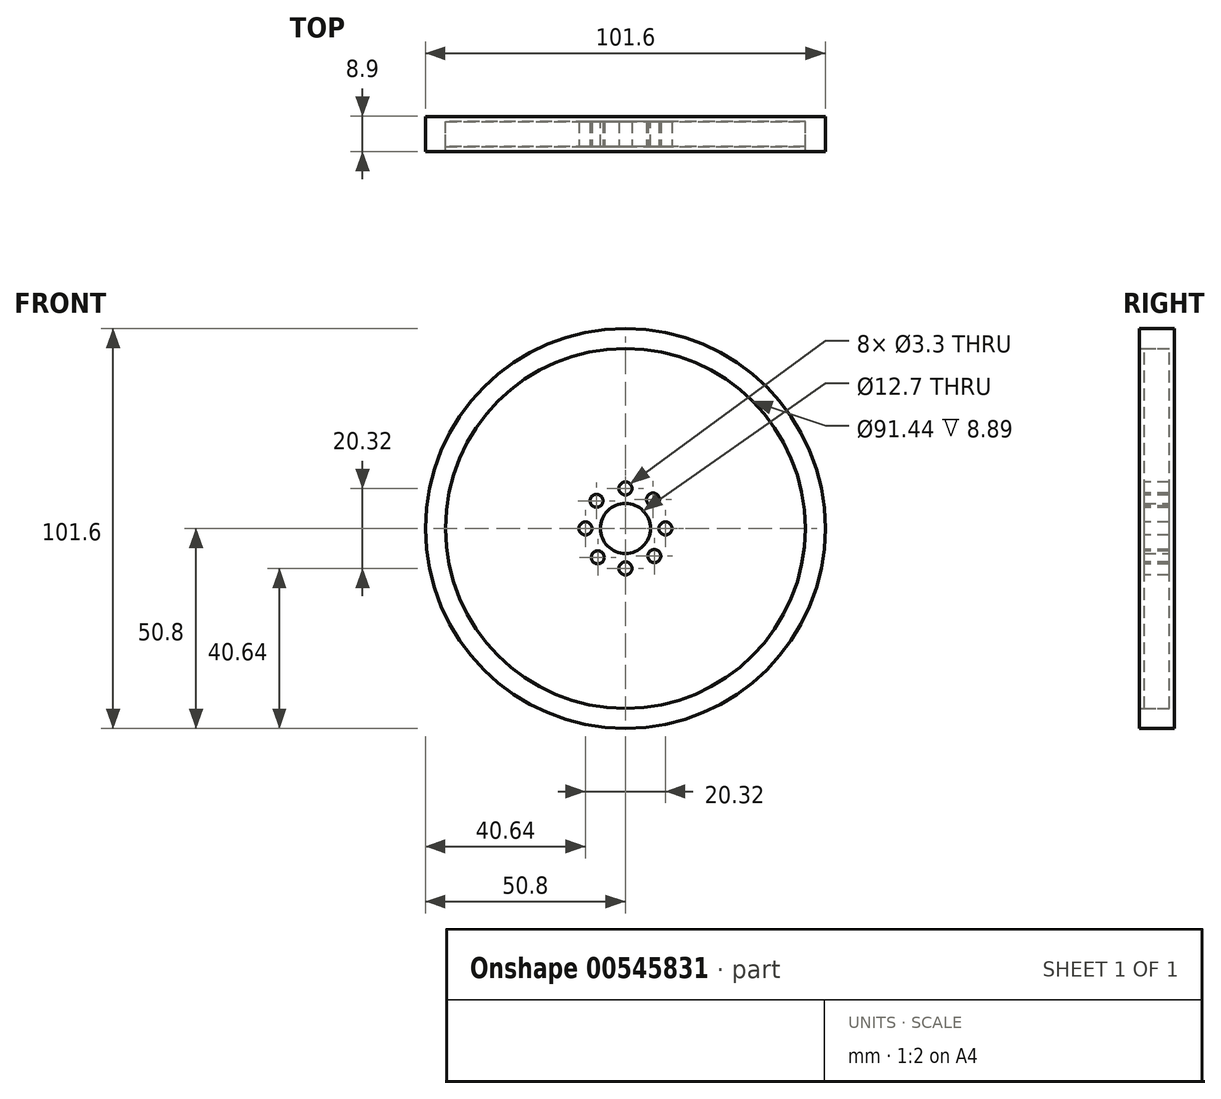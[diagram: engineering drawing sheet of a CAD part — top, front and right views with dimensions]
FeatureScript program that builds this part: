
annotation { "Feature Type Name" : "Feature", "Feature Type Description" : "" }
export const myFeature = defineFeature(function(context is Context, id is Id, definition is map)
    precondition{}
    {
        {
            var Q0;
            Q0=qCreatedBy(makeId("Front.planeOp"),FACE);
            var sketch = newSketch(context, id + "F0", { "sketchPlane" : qUnion([Q0])});
            skCircle(sketch, "E0", {"center": v(0, 0) * mm, "radius": 45.72 * mm});
            skCircle(sketch, "E1", {"center": v(0, 0) * mm, "radius": 50.8 * mm});
            skCircle(sketch, "E2", {"center": v(0, 0) * mm, "radius": 6.35 * mm});
            skSolve(sketch);
        }
        {
            var Q0;
            Q0=makeQuery(id+"F0.imprint","IMPRINT",FACE,{"disambiguationData":[TD([[makeQuery(id+"F0.imprint","IMPRINT",EDGE,{"derivedFrom":sQuery(id+"F0.wireOp",EDGE,"E0")}),-1.0]])]});
            extrude(context, id + "F1", {"entities" : qUnion([Q0]), "depth" : 8.9 * mm, "offsetDistance" : 25.4 * mm, "symmetric" : true});
        }
        {
            var Q0;
            Q0=makeQuery(id+"F0.imprint","IMPRINT",FACE,{"disambiguationData":[TD([[makeQuery(id+"F0.imprint","IMPRINT",EDGE,{"derivedFrom":sQuery(id+"F0.wireOp",EDGE,"E0")}),1.0]])]});
            extrude(context, id + "F2", {"entities" : qUnion([Q0]), "depth" : 6.35 * mm, "offsetDistance" : 25.4 * mm, "symmetric" : true});
        }
        {
            var Q0;
            Q0=makeQuery(id+"F2.opExtrude","CAP_FACE",FACE,{"disambiguationData":[OSD([sQuery(id+"F0.wireOp",EDGE,"E0"),sQuery(id+"F0.wireOp",EDGE,"E2")])],"isStart":false});
            var sketch = newSketch(context, id + "F3", { "sketchPlane" : qUnion([Q0])});
            skCircle(sketch, "E3", {"center": v(0, 0) * mm, "radius": 10.16 * mm, "construction": true});
            skPoint(sketch, "E4", {"position": v(0, 10.16) * mm});
            skPoint(sketch, "E5.2.0", {"position": v(7.02, 7.34) * mm});
            skPoint(sketch, "E6", {"position": v(10.16, 0) * mm});
            skPoint(sketch, "E7", {"position": v(0, -10.16) * mm});
            skPoint(sketch, "E8", {"position": v(-10.16, 0) * mm});
            skPoint(sketch, "E9.1.0", {"position": v(7.34, -7.02) * mm});
            skPoint(sketch, "E10.2.0", {"position": v(-7.02, -7.34) * mm});
            skPoint(sketch, "E11.1.0", {"position": v(-7.34, 7.02) * mm});
            skLineSegment(sketch, "E12", {"start": v(-7.02, -7.34) * mm, "end": v(0, 0) * mm, "construction": true});
            skLineSegment(sketch, "E13", {"start": v(-7.34, 7.02) * mm, "end": v(0, 0) * mm, "construction": true});
            skLineSegment(sketch, "E14", {"start": v(7.02, 7.34) * mm, "end": v(0, 0) * mm, "construction": true});
            skLineSegment(sketch, "E15", {"start": v(0, 0) * mm, "end": v(7.34, -7.02) * mm, "construction": true});
            skSolve(sketch);
        }
        {
            var Q0;
            Q0=sQuery(id+"F3.wireOp",VERTEX,"E6");
            var Q1;
            Q1=sQuery(id+"F3.wireOp",VERTEX,"E9.1.0");
            var Q2;
            Q2=sQuery(id+"F3.wireOp",VERTEX,"E9.2.0");
            var Q3;
            Q3=sQuery(id+"F3.wireOp",VERTEX,"E7");
            var Q4;
            Q4=sQuery(id+"F3.wireOp",VERTEX,"E10.1.0");
            var Q5;
            Q5=sQuery(id+"F3.wireOp",VERTEX,"E10.2.0");
            var Q6;
            Q6=sQuery(id+"F3.wireOp",VERTEX,"E8");
            var Q7;
            Q7=sQuery(id+"F3.wireOp",VERTEX,"E11.1.0");
            var Q8;
            Q8=sQuery(id+"F3.wireOp",VERTEX,"E11.2.0");
            var Q9;
            Q9=sQuery(id+"F3.wireOp",VERTEX,"E4");
            var Q10;
            Q10=sQuery(id+"F3.wireOp",VERTEX,"E5.1.0");
            var Q11;
            Q11=sQuery(id+"F3.wireOp",VERTEX,"E5.2.0");
            var Q12;
            Q12=makeQuery(id+"F2.opExtrude","SWEPT_BODY",BODY,{"disambiguationData":[OSD([sQuery(id+"F0.wireOp",EDGE,"E0"),sQuery(id+"F0.wireOp",EDGE,"E2")])]});
            hole(context, id + "F4", {"style" : HoleStyle.SIMPLE, "endStyle" : HoleEndStyle.THROUGH, "standardTappedOrClearance" : lookupTablePath({ "standard" : "ISO", "fit" : "Normal", "size" : "M3", "type" : "Clearance" }), "standardBlindInLast" : lookupTablePath({ "fit" : "Standard", "standard" : "ISO", "size" : "M3", "type" : "Clearance" }), "holeDiameter" : 3.3 * mm, "isTappedThrough" : true, "tappedDepth" : 12.7 * mm, "tapClearance" : 3, "locations" : qUnion([Q0, Q1, Q2, Q3, Q4, Q5, Q6, Q7, Q8, Q9, Q10, Q11]), "scope" : qUnion([Q12])});
        }
    });
